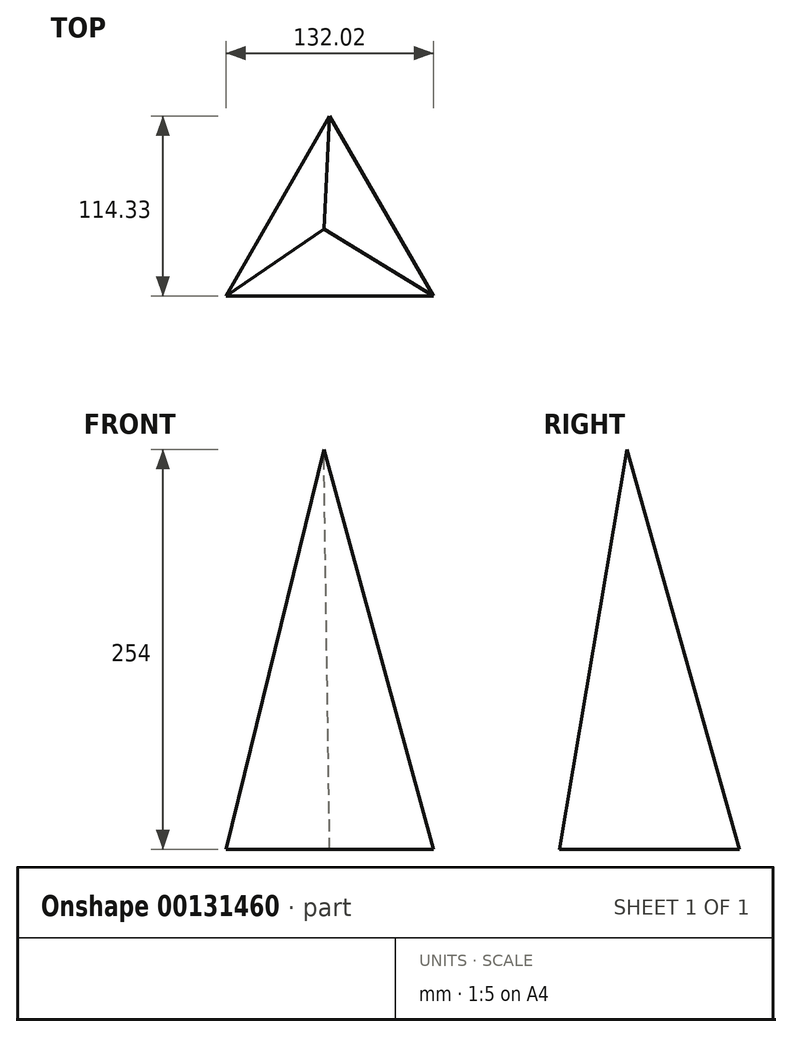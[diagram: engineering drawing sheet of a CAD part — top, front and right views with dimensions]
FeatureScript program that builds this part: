
annotation { "Feature Type Name" : "Feature", "Feature Type Description" : "" }
export const myFeature = defineFeature(function(context is Context, id is Id, definition is map)
    precondition{}
    {
        {
            var Q0;
            Q0=qCreatedBy(makeId("Top.planeOp"),FACE);
            var sketch = newSketch(context, id + "F0", { "sketchPlane" : qUnion([Q0])});
            skCircle(sketch, "E0.cCircle", {"center": v(0, 0) * mm, "radius": 76.22 * mm, "construction": true});
            skLineSegment(sketch, "E0.0", {"start": v(0, 76.22) * mm, "end": v(66, -38.11) * mm});
            skLineSegment(sketch, "E0.1", {"start": v(66, -38.11) * mm, "end": v(-66, -38.11) * mm});
            skLineSegment(sketch, "E0.2", {"start": v(-66, -38.11) * mm, "end": v(0, 76.22) * mm});
            skSolve(sketch);
        }
        {
            var Q0;
            Q0=qCreatedBy(makeId("Top.planeOp"),FACE);
            cPlane(context, id + "F1", {"entities" : qUnion([Q0]), "cplaneType" : CPlaneType.OFFSET, "offset" : 254 * mm, "width" : 152.4 * mm, "height" : 152.4 * mm});
        }
        {
            var Q0;
            Q0=qCreatedBy(id+"F1.planeOp",FACE);
            var sketch = newSketch(context, id + "F2", { "sketchPlane" : qUnion([Q0])});
            skPoint(sketch, "E1", {"position": v(-3.79, 4.52) * mm});
            skSolve(sketch);
        }
        {
            var Q0;
            Q0=makeQuery(id+"F0.imprint","IMPRINT",FACE,{"disambiguationData":[TD([[makeQuery(id+"F0.imprint","IMPRINT",EDGE,{"derivedFrom":sQuery(id+"F0.wireOp",EDGE,"E0.0")}),-1.0]])]});
            var Q1;
            Q1=sQuery(id+"F2.wireOp",VERTEX,"E1");
            loft(context, id + "F3", {"sheetProfilesArray" : [{ "sheetProfileEntities" : qUnion([Q0]) }, { "sheetProfileEntities" : qUnion([Q1]) }]});
        }
    });
